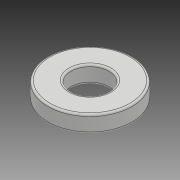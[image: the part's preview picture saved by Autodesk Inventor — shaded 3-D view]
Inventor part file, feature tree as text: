
AUTODESK INVENTOR PART (.ipt)
format: ipt  version: 2018 (Build 220112000, 112)  size: 116,736 bytes
history: native  units: mm
features: other x1, extrude x1, fillet x1, sketch x1
ambient origin geometry x8: Origin, YZ Plane, XZ Plane, XY Plane, X Axis, Y Axis, Z Axis, Center Point
bodies: Body1 (feature_tree)
feature tree (4):
  other  "ソリッド1"
  extrude  "押し出し1"  Depth=15.875mm
  fillet  "フィレット1"  Radius=34.925mm
  sketch  "スケッチ1"
